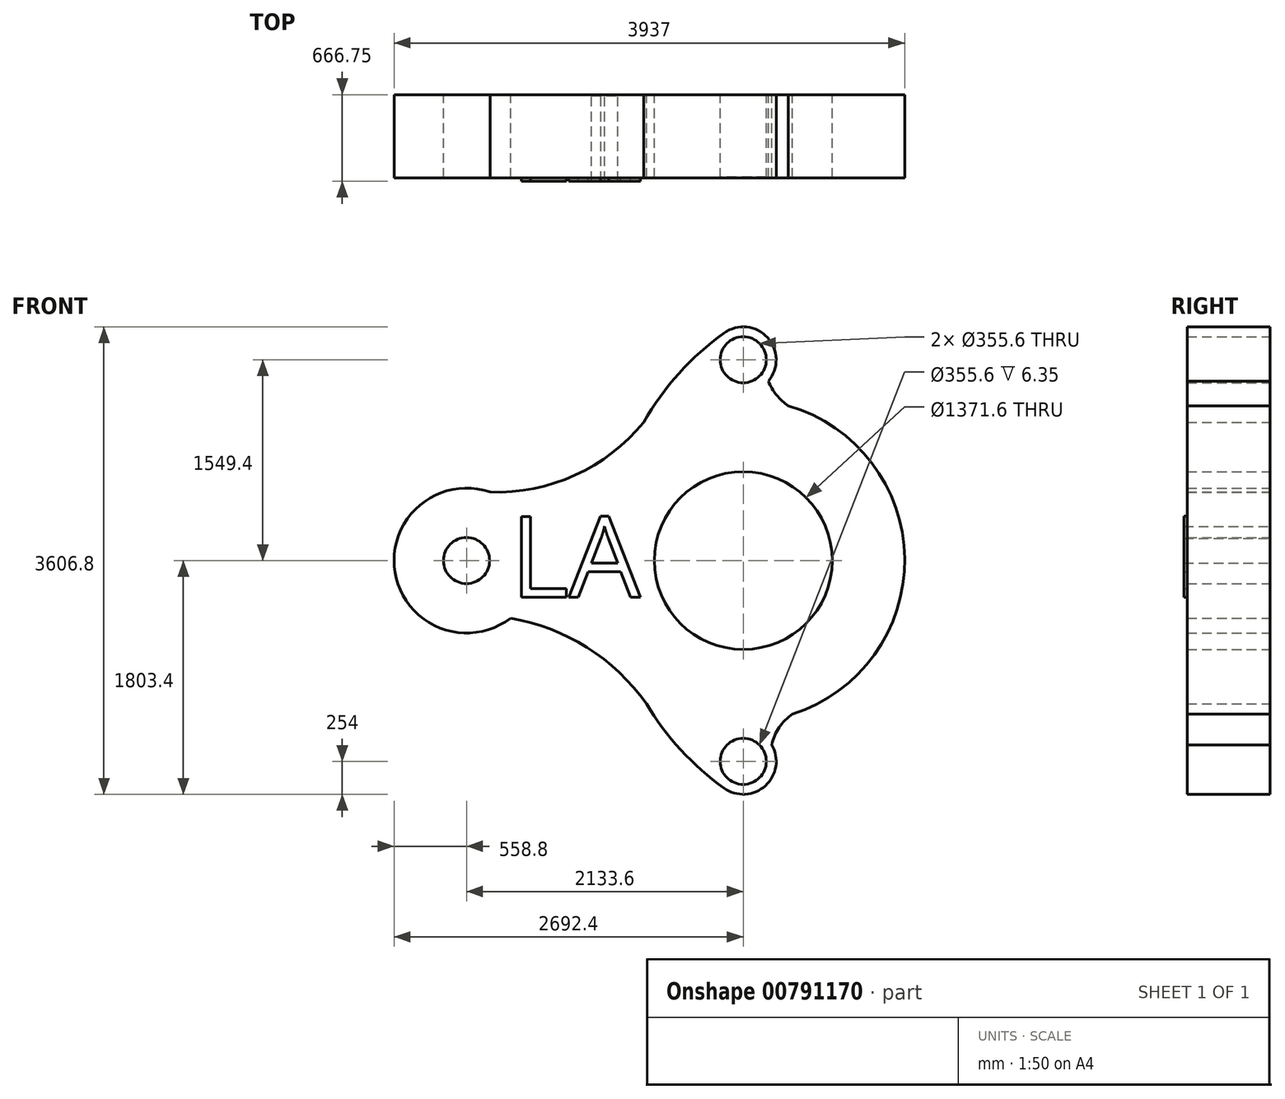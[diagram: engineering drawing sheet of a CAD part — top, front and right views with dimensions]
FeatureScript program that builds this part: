
annotation { "Feature Type Name" : "Feature", "Feature Type Description" : "" }
export const myFeature = defineFeature(function(context is Context, id is Id, definition is map)
    precondition{}
    {
        {
            var Q0;
            Q0=qCreatedBy(makeId("Front.planeOp"),FACE);
            var sketch = newSketch(context, id + "F0", { "sketchPlane" : qUnion([Q0])});
            skArc(sketch, "E0", {"start": v(380.04, -1185.16) * mm, "mid": v(1244.49, 16.58) * mm, "end": v(348.34, 1194.86) * mm});
            skCircle(sketch, "E1", {"center": v(0, 0) * mm, "radius": 685.8 * mm});
            skLineSegment(sketch, "E2", {"start": v(0, 0) * mm, "end": v(-2133.6, 0) * mm});
            skLineSegment(sketch, "E3", {"start": v(0, 0) * mm, "end": v(0, 1549.4) * mm});
            skLineSegment(sketch, "E4", {"start": v(0, 0) * mm, "end": v(0, -1549.4) * mm});
            skCircle(sketch, "E5", {"center": v(0, 1549.4) * mm, "radius": 177.8 * mm});
            skCircle(sketch, "E6", {"center": v(0, 1549.4) * mm, "radius": 254 * mm});
            skCircle(sketch, "E7", {"center": v(-2133.6, 0) * mm, "radius": 177.8 * mm});
            skArc(sketch, "E8", {"start": v(-1953.16, 528.87) * mm, "mid": v(-2685.1, -90.06) * mm, "end": v(-1794.3, -444) * mm});
            skCircle(sketch, "E9", {"center": v(0, -1549.4) * mm, "radius": 177.8 * mm});
            skCircle(sketch, "E10", {"center": v(0, -1549.4) * mm, "radius": 254 * mm});
            skArc(sketch, "E11", {"start": v(-147.78, 1755.99) * mm, "mid": v(-495.26, 1445.6) * mm, "end": v(-768.07, 1067.9) * mm});
            skArc(sketch, "E12", {"start": v(-1953.16, 528.87) * mm, "mid": v(-1297.05, 658.65) * mm, "end": v(-768.07, 1067.9) * mm});
            skArc(sketch, "E13", {"start": v(-746.8, -1104.43) * mm, "mid": v(-1204.89, -670.07) * mm, "end": v(-1794.3, -444) * mm});
            skArc(sketch, "E14", {"start": v(193.07, 1384.36) * mm, "mid": v(256.32, 1277.82) * mm, "end": v(348.34, 1194.86) * mm});
            skArc(sketch, "E15", {"start": v(380.04, -1185.16) * mm, "mid": v(276.13, -1287.44) * mm, "end": v(219.67, -1421.87) * mm});
            skArc(sketch, "E16.trimOffspring", {"start": v(-746.8, -1104.43) * mm, "mid": v(-481.04, -1461.24) * mm, "end": v(-147.78, -1755.99) * mm});
            skSolve(sketch);
        }
        {
            var Q0;
            Q0=makeQuery(id+"F0.imprint","IMPRINT",FACE,{"disambiguationData":[TD([[makeQuery(id+"F0.imprint","IMPRINT",EDGE,{"derivedFrom":sQuery(id+"F0.wireOp",EDGE,"E7")}),-1.0]])]});
            var Q1;
            Q1=makeQuery(id+"F0.imprint","IMPRINT",FACE,{"disambiguationData":[TD([[makeQuery(id+"F0.imprint","IMPRINT",EDGE,{"derivedFrom":sQuery(id+"F0.wireOp",EDGE,"E0")}),1.0]])]});
            var Q2;
            Q2=makeQuery(id+"F0.imprint","IMPRINT",FACE,{"disambiguationData":[TD([[makeQuery(id+"F0.imprint","IMPRINT",EDGE,{"derivedFrom":sQuery(id+"F0.wireOp",EDGE,"E5")}),-1.0]])]});
            var Q3;
            Q3=makeQuery(id+"F0.imprint","IMPRINT",FACE,{"disambiguationData":[TD([[makeQuery(id+"F0.imprint","IMPRINT",EDGE,{"derivedFrom":sQuery(id+"F0.wireOp",EDGE,"E9")}),-1.0]])]});
            extrude(context, id + "F1", {"entities" : qUnion([Q0, Q1, Q2, Q3]), "depth" : 6.35 * mm, "offsetDistance" : 25.4 * mm});
        }
        {
            var Q0;
            Q0=makeQuery(id+"F1.opExtrude","CAP_FACE",FACE,{"disambiguationData":[OSD([sQuery(id+"F0.wireOp",EDGE,"E0"),sQuery(id+"F0.wireOp",EDGE,"E1"),sQuery(id+"F0.wireOp",EDGE,"E5"),sQuery(id+"F0.wireOp",EDGE,"E6"),sQuery(id+"F0.wireOp",EDGE,"E7"),sQuery(id+"F0.wireOp",EDGE,"E8"),sQuery(id+"F0.wireOp",EDGE,"E9"),sQuery(id+"F0.wireOp",EDGE,"E10"),sQuery(id+"F0.wireOp",EDGE,"E11"),sQuery(id+"F0.wireOp",EDGE,"E12"),sQuery(id+"F0.wireOp",EDGE,"E13"),sQuery(id+"F0.wireOp",EDGE,"E14"),sQuery(id+"F0.wireOp",EDGE,"E15"),sQuery(id+"F0.wireOp",EDGE,"E16.trimOffspring")])],"isStart":false});
            var sketch = newSketch(context, id + "F2", { "sketchPlane" : qUnion([Q0])});
            skText(sketch, "E17", { "text": "LA", "fontName": "OpenSans-Regular.ttf"});
            const initialGuessF2  = {"E17": [-1.7967, -0.28267, 1, 0, 0.62665]};
            skSetInitialGuess(sketch, initialGuessF2);
            skSolve(sketch);
        }
        {
            var Q0;
            Q0 = qSketchRegion(id + "F2", true);
            extrude(context, id + "F3", {"entities" : qUnion([Q0]), "operationType" : NewBodyOperationType.ADD, "depth" : 25.4 * mm, "offsetDistance" : 25.4 * mm});
        }
        {
            var Q0;
            Q0=makeQuery(id+"F0.imprint","IMPRINT",FACE,{"disambiguationData":[TD([[makeQuery(id+"F0.imprint","IMPRINT",EDGE,{"derivedFrom":sQuery(id+"F0.wireOp",EDGE,"E9")}),1.0]])]});
            var Q1;
            {var subQ0=sQuery(id+"F0.wireOp",EDGE,"E16.trimOffspring");var subQ1=sQuery(id+"F0.wireOp",EDGE,"E15");var subQ2=sQuery(id+"F0.wireOp",EDGE,"E14");var subQ3=sQuery(id+"F0.wireOp",EDGE,"E13");var subQ4=sQuery(id+"F0.wireOp",EDGE,"E5");var subQ5=sQuery(id+"F0.wireOp",EDGE,"E1");var subQ6=sQuery(id+"F0.wireOp",EDGE,"E6");var subQ7=sQuery(id+"F0.wireOp",EDGE,"E0");var subQ8=sQuery(id+"F0.wireOp",EDGE,"E12");var subQ9=sQuery(id+"F0.wireOp",EDGE,"E7");var subQ10=sQuery(id+"F0.wireOp",EDGE,"E8");var subQ11=sQuery(id+"F0.wireOp",EDGE,"E9");var subQ12=sQuery(id+"F0.wireOp",EDGE,"E10");var subQ13=sQuery(id+"F0.wireOp",EDGE,"E11");Q1=makeQuery(id+"F3.boolean.opBoolean","SPLIT",FACE,{"disambiguationData":[TD([makeQuery(id+"F1.opExtrude","SWEPT_FACE",FACE,{"disambiguationData":[OSD([subQ7])]})])],"derivedFrom":makeQuery(id+"F1.opExtrude","CAP_FACE",FACE,{"disambiguationData":[OSD([subQ7,subQ5,subQ4,subQ6,subQ9,subQ10,subQ11,subQ12,subQ13,subQ8,subQ3,subQ2,subQ1,subQ0])],"isStart":false})});}
            var Q2;
            Q2=makeQuery(id+"F3.opExtrude","CAP_FACE",FACE,{"disambiguationData":[OSD([sQuery(id+"F2.wireOp",EDGE,"E17.sketch_text.stroke-0"),sQuery(id+"F2.wireOp",EDGE,"E17.sketch_text.stroke-1"),sQuery(id+"F2.wireOp",EDGE,"E17.sketch_text.stroke-2"),sQuery(id+"F2.wireOp",EDGE,"E17.sketch_text.stroke-3"),sQuery(id+"F2.wireOp",EDGE,"E17.sketch_text.stroke-4"),sQuery(id+"F2.wireOp",EDGE,"E17.sketch_text.stroke-5")])],"isStart":false});
            var Q3;
            Q3=makeQuery(id+"F3.opExtrude","CAP_FACE",FACE,{"disambiguationData":[OSD([sQuery(id+"F2.wireOp",EDGE,"E17.sketch_text.stroke-6"),sQuery(id+"F2.wireOp",EDGE,"E17.sketch_text.stroke-7"),sQuery(id+"F2.wireOp",EDGE,"E17.sketch_text.stroke-8"),sQuery(id+"F2.wireOp",EDGE,"E17.sketch_text.stroke-9"),sQuery(id+"F2.wireOp",EDGE,"E17.sketch_text.stroke-10"),sQuery(id+"F2.wireOp",EDGE,"E17.sketch_text.stroke-11"),sQuery(id+"F2.wireOp",EDGE,"E17.sketch_text.stroke-12"),sQuery(id+"F2.wireOp",EDGE,"E17.sketch_text.stroke-13"),sQuery(id+"F2.wireOp",EDGE,"E17.sketch_text.stroke-14"),sQuery(id+"F2.wireOp",EDGE,"E17.sketch_text.stroke-15"),sQuery(id+"F2.wireOp",EDGE,"E17.sketch_text.stroke-16"),sQuery(id+"F2.wireOp",EDGE,"E17.sketch_text.stroke-17"),sQuery(id+"F2.wireOp",EDGE,"E17.sketch_text.stroke-18")])],"isStart":false});
            extrude(context, id + "F4", {"entities" : qUnion([Q0, Q1, Q2, Q3]), "operationType" : NewBodyOperationType.ADD, "depth" : 635 * mm, "offsetDistance" : 25.4 * mm});
        }
        {
            var Q0;
            Q0=makeQuery(id+"F4.opExtrude","CAP_FACE",FACE,{"disambiguationData":[OSD([sQuery(id+"F0.wireOp",EDGE,"E9")])],"isStart":false});
            extrude(context, id + "F5", {"entities" : qUnion([Q0]), "operationType" : NewBodyOperationType.ADD, "oppositeDirection" : true, "depth" : 25.4 * mm, "offsetDistance" : 25.4 * mm});
        }
        {
            var Q0;
            Q0=makeQuery(id+"F4.opExtrude","CAP_FACE",FACE,{"disambiguationData":[OSD([sQuery(id+"F0.wireOp",EDGE,"E9")])],"isStart":false});
            extrude(context, id + "F6", {"entities" : qUnion([Q0]), "operationType" : NewBodyOperationType.ADD, "oppositeDirection" : true, "depth" : 25.4 * mm, "offsetDistance" : 25.4 * mm});
        }
    });
